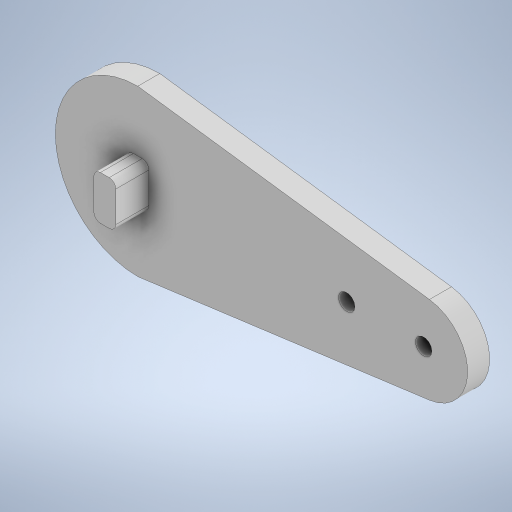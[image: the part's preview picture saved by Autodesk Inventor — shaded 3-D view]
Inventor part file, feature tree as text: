
AUTODESK INVENTOR PART (.ipt)
format: ipt  version: 2024.2 (Build 282272000, 272)  size: 258,048 bytes
history: native  units: mm
features: extrude x2, other x1, sketch x1, fillet x1
ambient origin geometry x8: Origin, YZ Plane, XZ Plane, XY Plane, X Axis, Y Axis, Z Axis, Center Point
bodies: Body1 (feature_tree)
feature tree (5):
  other  "Bryła1"
  sketch  "Szkic1"
  extrude  "Wyciągnięcie proste1"  Depth=15.0mm
  extrude  "Wyciągnięcie proste2"  Depth=2.0mm
  fillet  "Zaokrąglenie1"  Radius=4.0mm
